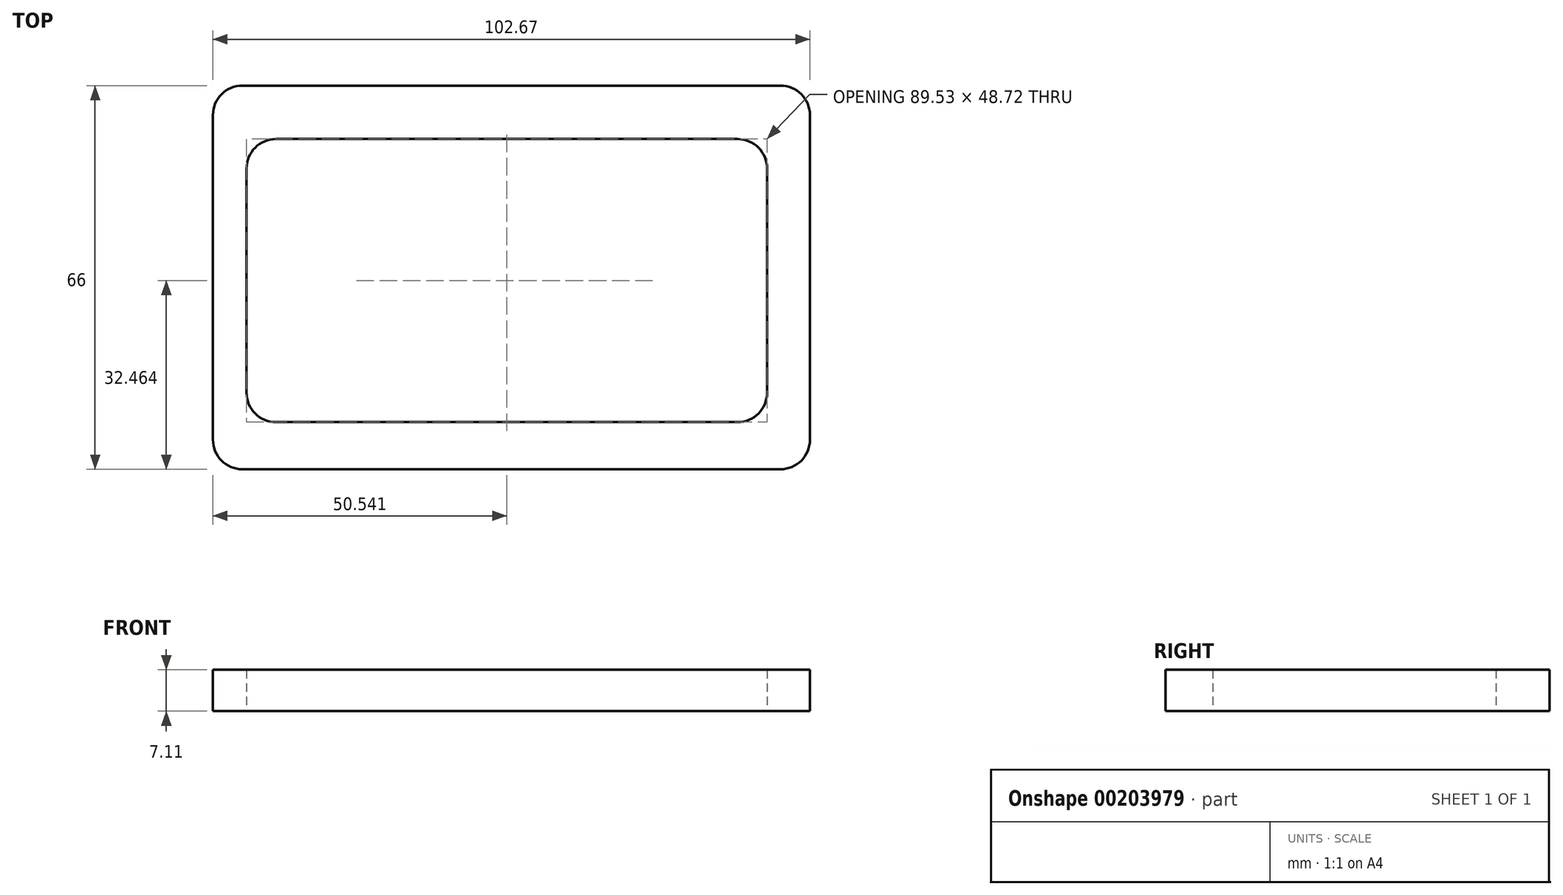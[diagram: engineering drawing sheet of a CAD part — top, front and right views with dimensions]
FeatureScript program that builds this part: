
annotation { "Feature Type Name" : "Feature", "Feature Type Description" : "" }
export const myFeature = defineFeature(function(context is Context, id is Id, definition is map)
    precondition{}
    {
        {
            var Q0;
            Q0=qCreatedBy(makeId("Top.planeOp"),FACE);
            var sketch = newSketch(context, id + "F0", { "sketchPlane" : qUnion([Q0])});
            skLineSegment(sketch, "E0.bottom", {"start": v(-50.46, 21.76) * mm, "end": v(52.21, 21.76) * mm});
            skLineSegment(sketch, "E0.top", {"start": v(-50.46, -44.24) * mm, "end": v(52.21, -44.24) * mm});
            skLineSegment(sketch, "E0.left", {"start": v(-50.46, 21.76) * mm, "end": v(-50.46, -44.24) * mm});
            skLineSegment(sketch, "E0.right", {"start": v(52.21, 21.76) * mm, "end": v(52.21, -44.24) * mm});
            skSolve(sketch);
        }
        {
            var Q0;
            Q0 = qSketchRegion(id + "F0", true);
            extrude(context, id + "F1", {"entities" : qUnion([Q0]), "depth" : 7.11 * mm});
        }
        {
            var Q0;
            Q0=makeQuery(id+"F1.opExtrude","CAP_FACE",FACE,{"disambiguationData":[OSD([sQuery(id+"F0.wireOp",EDGE,"E0.bottom"),sQuery(id+"F0.wireOp",EDGE,"E0.top"),sQuery(id+"F0.wireOp",EDGE,"E0.left"),sQuery(id+"F0.wireOp",EDGE,"E0.right")])],"isStart":true});
            var sketch = newSketch(context, id + "F2", { "sketchPlane" : qUnion([Q0])});
            skLineSegment(sketch, "E1.bottom", {"start": v(-44.68, 36.13) * mm, "end": v(44.84, 36.13) * mm});
            skLineSegment(sketch, "E1.top", {"start": v(-44.68, -12.58) * mm, "end": v(44.84, -12.58) * mm});
            skLineSegment(sketch, "E1.left", {"start": v(-44.68, 36.13) * mm, "end": v(-44.68, -12.58) * mm});
            skLineSegment(sketch, "E1.right", {"start": v(44.84, 36.13) * mm, "end": v(44.84, -12.58) * mm});
            skSolve(sketch);
        }
        {
            var Q0;
            Q0 = qSketchRegion(id + "F2", true);
            var Q1;
            Q1=makeQuery(id+"F1.opExtrude","CAP_FACE",FACE,{"disambiguationData":[OSD([sQuery(id+"F0.wireOp",EDGE,"E0.bottom"),sQuery(id+"F0.wireOp",EDGE,"E0.top"),sQuery(id+"F0.wireOp",EDGE,"E0.left"),sQuery(id+"F0.wireOp",EDGE,"E0.right")])],"isStart":false});
            extrude(context, id + "F3", {"entities" : qUnion([Q0, Q1]), "operationType" : NewBodyOperationType.REMOVE, "endBound" : BoundingType.THROUGH_ALL, "oppositeDirection" : true, "depth" : 25.4 * mm});
        }
        {
            var Q0;
            Q0=makeQuery(id+"F1.opExtrude","SWEPT_EDGE",EDGE,{"disambiguationData":[OSD([sQuery(id+"F0.wireOp",EDGE,"E0.bottom"),sQuery(id+"F0.wireOp",EDGE,"E0.left")])]});
            var Q1;
            Q1=makeQuery(id+"F1.opExtrude","SWEPT_EDGE",EDGE,{"disambiguationData":[OSD([sQuery(id+"F0.wireOp",EDGE,"E0.bottom"),sQuery(id+"F0.wireOp",EDGE,"E0.right")])]});
            var Q2;
            Q2=makeQuery(id+"F1.opExtrude","SWEPT_EDGE",EDGE,{"disambiguationData":[OSD([sQuery(id+"F0.wireOp",EDGE,"E0.top"),sQuery(id+"F0.wireOp",EDGE,"E0.right")])]});
            var Q3;
            Q3=makeQuery(id+"F1.opExtrude","SWEPT_EDGE",EDGE,{"disambiguationData":[OSD([sQuery(id+"F0.wireOp",EDGE,"E0.top"),sQuery(id+"F0.wireOp",EDGE,"E0.left")])]});
            var Q4;
            Q4=makeQuery(id+"F3.boolean.opBoolean","COPY",EDGE,{"derivedFrom":makeQuery(id+"F3.opExtrude","SWEPT_EDGE",EDGE,{"disambiguationData":[OSD([sQuery(id+"F2.wireOp",EDGE,"E1.bottom"),sQuery(id+"F2.wireOp",EDGE,"E1.left")])]})});
            var Q5;
            Q5=makeQuery(id+"F3.boolean.opBoolean","COPY",EDGE,{"derivedFrom":makeQuery(id+"F3.opExtrude","SWEPT_EDGE",EDGE,{"disambiguationData":[OSD([sQuery(id+"F2.wireOp",EDGE,"E1.top"),sQuery(id+"F2.wireOp",EDGE,"E1.left")])]})});
            var Q6;
            Q6=makeQuery(id+"F3.boolean.opBoolean","COPY",EDGE,{"derivedFrom":makeQuery(id+"F3.opExtrude","SWEPT_EDGE",EDGE,{"disambiguationData":[OSD([sQuery(id+"F2.wireOp",EDGE,"E1.top"),sQuery(id+"F2.wireOp",EDGE,"E1.right")])]})});
            var Q7;
            Q7=makeQuery(id+"F3.boolean.opBoolean","COPY",EDGE,{"derivedFrom":makeQuery(id+"F3.opExtrude","SWEPT_EDGE",EDGE,{"disambiguationData":[OSD([sQuery(id+"F2.wireOp",EDGE,"E1.bottom"),sQuery(id+"F2.wireOp",EDGE,"E1.right")])]})});
            fillet(context, id + "F4", {"entities" : qUnion([Q0, Q1, Q2, Q3, Q4, Q5, Q6, Q7]), "radius" : 5.08 * mm, "tangentPropagation" : true, "allowEdgeOverflow" : false});
        }
    });
